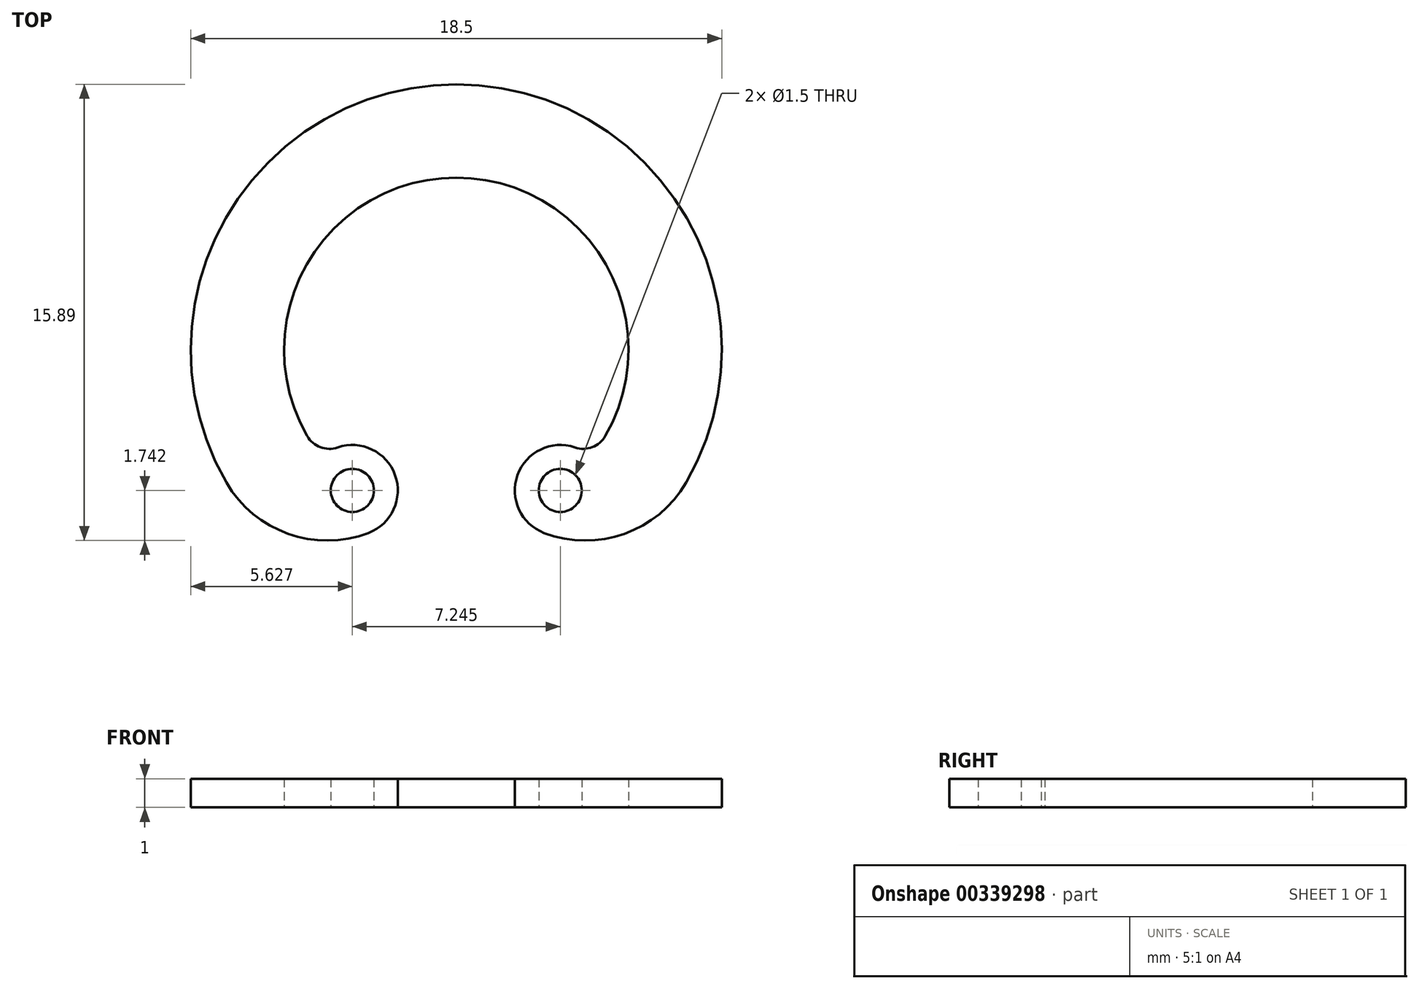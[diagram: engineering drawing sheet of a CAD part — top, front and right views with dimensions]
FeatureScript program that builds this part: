
annotation { "Feature Type Name" : "Feature", "Feature Type Description" : "" }
export const myFeature = defineFeature(function(context is Context, id is Id, definition is map)
    precondition{}
    {
        {
            var Q0;
            Q0=qCreatedBy(makeId("Top.planeOp"),FACE);
            var sketch = newSketch(context, id + "F0", { "sketchPlane" : qUnion([Q0])});
            skCircle(sketch, "E0", {"center": v(0, 0) * mm, "radius": 9.25 * mm, "construction": true});
            skCircle(sketch, "E1", {"center": v(0, 0) * mm, "radius": 6 * mm, "construction": true});
            skLineSegment(sketch, "E2", {"start": v(0, 6) * mm, "end": v(15.31, 6) * mm, "construction": true});
            skLineSegment(sketch, "E3", {"start": v(0, 6) * mm, "end": v(-12.46, 6) * mm, "construction": true});
            skLineSegment(sketch, "E4", {"start": v(0, 9.25) * mm, "end": v(12.89, 9.25) * mm, "construction": true});
            skLineSegment(sketch, "E5", {"start": v(0, 9.25) * mm, "end": v(-12.37, 9.25) * mm, "construction": true});
            skCircle(sketch, "E6", {"center": v(0, 0) * mm, "radius": 4.5 * mm, "construction": true});
            skLineSegment(sketch, "E7", {"start": v(0, 0) * mm, "end": v(-13.02, -7.52) * mm, "construction": true});
            skLineSegment(sketch, "E8.MirrorCS", {"start": v(0, 0) * mm, "end": v(13.02, -7.52) * mm, "construction": true});
            skArc(sketch, "E9", {"start": v(5.2, -3) * mm, "mid": v(0, 6) * mm, "end": v(-5.2, -3) * mm});
            skArc(sketch, "E10", {"start": v(8.01, -4.63) * mm, "mid": v(0, 9.25) * mm, "end": v(-8.01, -4.63) * mm});
            skArc(sketch, "E11", {"start": v(-5.2, -3) * mm, "mid": v(-4.74, -3.4) * mm, "end": v(-4.13, -3.4) * mm});
            skArc(sketch, "E12", {"start": v(-4.13, -3.4) * mm, "mid": v(-2.13, -4.36) * mm, "end": v(-3.06, -6.38) * mm});
            skArc(sketch, "E13", {"start": v(-3.06, -6.38) * mm, "mid": v(-5.86, -6.4) * mm, "end": v(-8.01, -4.63) * mm});
            skCircle(sketch, "E14", {"center": v(-3.62, -4.9) * mm, "radius": 0.75 * mm});
            skArc(sketch, "E15.MirrorCS", {"start": v(4.13, -3.4) * mm, "mid": v(2.13, -4.36) * mm, "end": v(3.06, -6.38) * mm});
            skCircle(sketch, "E16.MirrorC", {"center": v(3.62, -4.9) * mm, "radius": 0.75 * mm});
            skArc(sketch, "E17.MirrorCS", {"start": v(3.06, -6.38) * mm, "mid": v(5.86, -6.4) * mm, "end": v(8.01, -4.63) * mm});
            skArc(sketch, "E18.MirrorCS", {"start": v(5.2, -3) * mm, "mid": v(4.74, -3.4) * mm, "end": v(4.13, -3.4) * mm});
            skSolve(sketch);
        }
        {
            var Q0;
            Q0=qSketchRegion(id+"F0",true);
            extrude(context, id + "F1", {"entities" : qUnion([Q0]), "depth" : 1 * mm, "offsetDistance" : 25 * mm});
        }
    });
